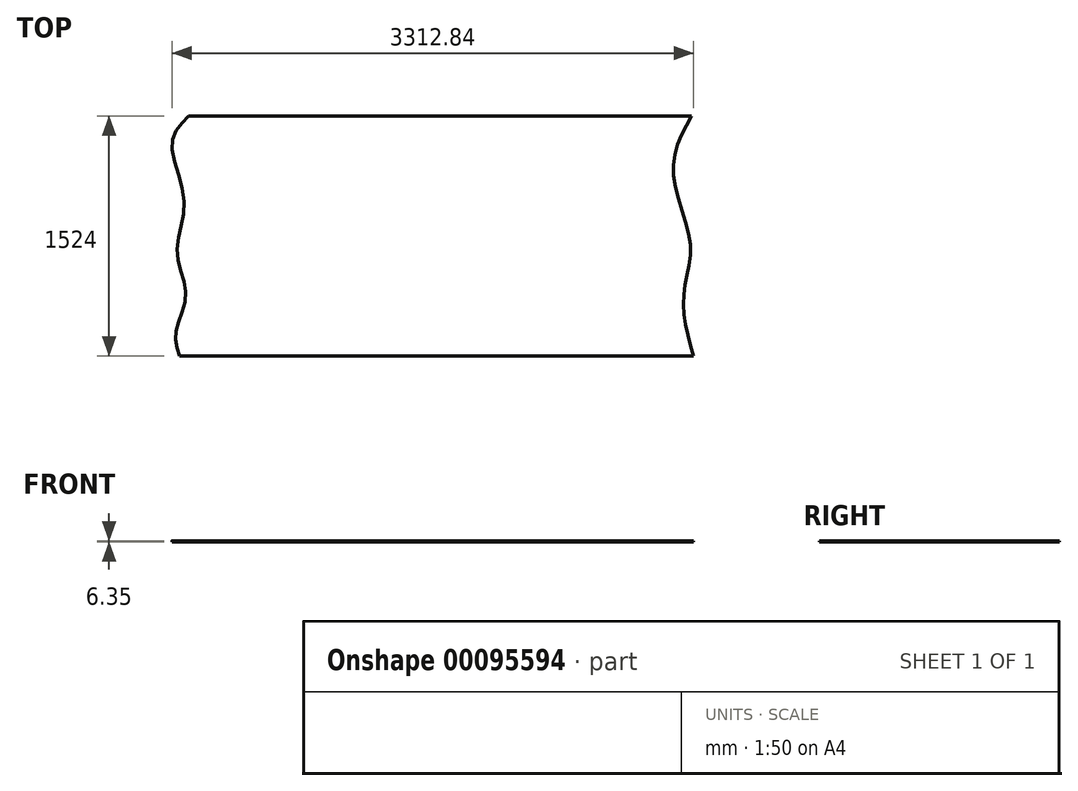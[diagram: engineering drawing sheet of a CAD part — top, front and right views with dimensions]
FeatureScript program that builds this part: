
annotation { "Feature Type Name" : "Feature", "Feature Type Description" : "" }
export const myFeature = defineFeature(function(context is Context, id is Id, definition is map)
    precondition{}
    {
        {
            var Q0;
            Q0=qCreatedBy(makeId("Top.planeOp"),FACE);
            var sketch = newSketch(context, id + "F0", { "sketchPlane" : qUnion([Q0])});
            skLineSegment(sketch, "E0.bottom", {"start": v(-1551.53, 762) * mm, "end": v(1641.73, 762) * mm});
            skLineSegment(sketch, "E0.top", {"start": v(-1609.26, -762) * mm, "end": v(1656.17, -762) * mm});
            skPoint(sketch, "E0.middle", {"position": v(0, 0) * mm});
            skFitSpline(sketch, "E1", {"points": [v(-1551.53, 762) * mm, v(-1656.17, 589.62) * mm, v(-1580.4, 214.36) * mm, v(-1623.7, -106.77) * mm, v(-1569.57, -373.77) * mm, v(-1630.91, -601.1) * mm, v(-1609.26, -762) * mm], "startDerivative": vector(-1010.45, -1008.79) * mm, "endDerivative": vector(354.52, -1172.48) * mm});
            skFitSpline(sketch, "E2", {"points": [v(1641.73, 762) * mm, v(1526.27, 409.2) * mm, v(1634.52, -52.64) * mm, v(1591.22, -395.42) * mm, v(1656.17, -762) * mm], "startDerivative": vector(-742.6, -1370.63) * mm, "endDerivative": vector(441.76, -1530.24) * mm});
            skPoint(sketch, "E0.left.start.orphan", {"position": v(-1750, 762) * mm});
            skPoint(sketch, "E3.orphan", {"position": v(-1750, -762) * mm});
            skPoint(sketch, "E0.right.start.orphan", {"position": v(1750, 762) * mm});
            skPoint(sketch, "E4.orphan", {"position": v(1750, -762) * mm});
            skSolve(sketch);
        }
        {
            var Q0;
            Q0 = qSketchRegion(id + "F0", true);
            extrude(context, id + "F1", {"entities" : qUnion([Q0]), "depth" : 6.35 * mm});
        }
    });
